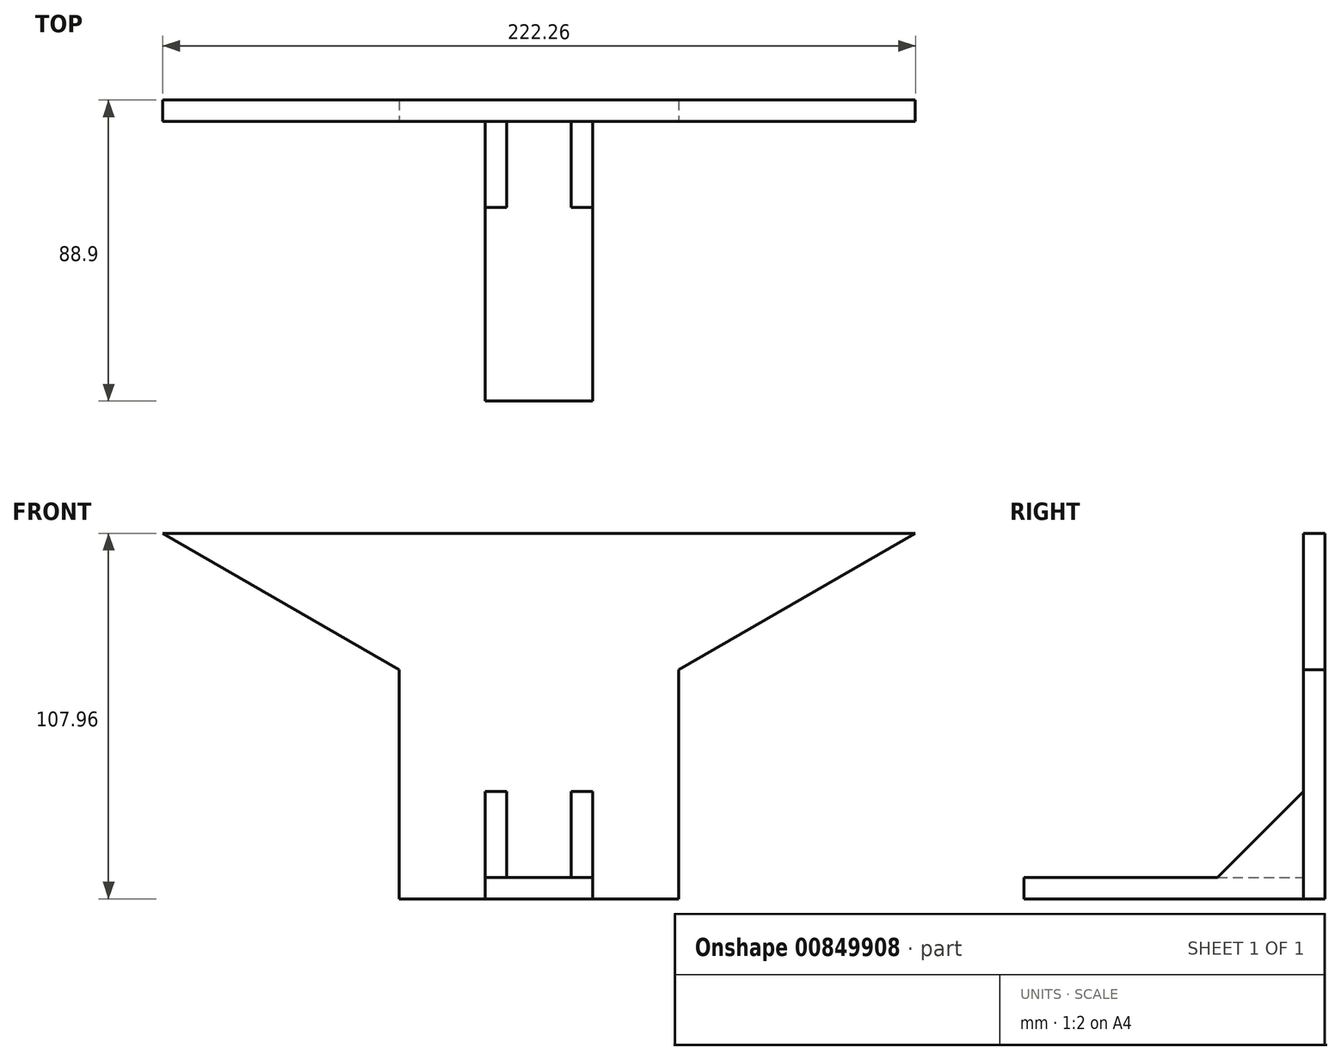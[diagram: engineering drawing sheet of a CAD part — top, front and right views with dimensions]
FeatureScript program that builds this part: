
annotation { "Feature Type Name" : "Feature", "Feature Type Description" : "" }
export const myFeature = defineFeature(function(context is Context, id is Id, definition is map)
    precondition{}
    {
        {
            var Q0;
            Q0=qCreatedBy(makeId("Front.planeOp"),FACE);
            var sketch = newSketch(context, id + "F0", { "sketchPlane" : qUnion([Q0])});
            skLineSegment(sketch, "E0.bottom", {"start": v(-41.28, 53.98) * mm, "end": v(0, 53.98) * mm});
            skLineSegment(sketch, "E0.top", {"start": v(-41.28, -53.98) * mm, "end": v(0, -53.98) * mm});
            skLineSegment(sketch, "E0.left", {"start": v(-41.28, 53.97) * mm, "end": v(-41.28, -53.98) * mm});
            skLineSegment(sketch, "E0.right", {"start": v(0, 53.98) * mm, "end": v(0, -53.98) * mm});
            skLineSegment(sketch, "E1", {"start": v(-41.28, 53.97) * mm, "end": v(-111.13, 53.97) * mm});
            skLineSegment(sketch, "E2", {"start": v(-111.12, 53.97) * mm, "end": v(-41.28, 13.65) * mm});
            skSolve(sketch);
        }
        {
            var Q0;
            {var subQ0=sQuery(id+"F0.wireOp",EDGE,"E1");Q0=makeQuery(id+"F0.imprint","IMPRINT",FACE,{"disambiguationData":[TD([[makeQuery(id+"F0.imprint","IMPRINT",EDGE,{"derivedFrom":subQ0}),1.0]])]});}
            var Q1;
            {var subQ3=sQuery(id+"F0.wireOp",EDGE,"E0.bottom");Q1=makeQuery(id+"F0.imprint","IMPRINT",FACE,{"disambiguationData":[TD([[makeQuery(id+"F0.imprint","IMPRINT",EDGE,{"derivedFrom":subQ3}),-1.0]])]});}
            extrude(context, id + "F1", {"entities" : qUnion([Q0, Q1]), "oppositeDirection" : true, "depth" : 6.35 * mm, "offsetDistance" : 25.4 * mm});
        }
        {
            var Q0;
            Q0=makeQuery(id+"F1.opExtrude","SWEPT_BODY",BODY,{"disambiguationData":[OSD([sQuery(id+"F0.wireOp",EDGE,"E0.bottom"),sQuery(id+"F0.wireOp",EDGE,"E0.top"),sQuery(id+"F0.wireOp",EDGE,"E0.left"),sQuery(id+"F0.wireOp",EDGE,"E0.right"),sQuery(id+"F0.wireOp",EDGE,"E1"),sQuery(id+"F0.wireOp",EDGE,"E2")])]});
            var Q1;
            Q1=qCreatedBy(makeId("Right.planeOp"),FACE);
            mirror(context, id + "F2", {"operationType" : NewBodyOperationType.ADD, "entities" : qUnion([Q0]), "mirrorPlane" : qUnion([Q1])});
        }
        {
            var Q0;
            Q0=qCreatedBy(makeId("Front.planeOp"),FACE);
            var sketch = newSketch(context, id + "F3", { "sketchPlane" : qUnion([Q0])});
            skLineSegment(sketch, "E3.bottom", {"start": v(-15.88, -47.62) * mm, "end": v(15.88, -47.62) * mm});
            skLineSegment(sketch, "E3.top", {"start": v(-15.88, -53.98) * mm, "end": v(15.88, -53.98) * mm});
            skLineSegment(sketch, "E3.left", {"start": v(-15.88, -47.62) * mm, "end": v(-15.88, -53.98) * mm});
            skLineSegment(sketch, "E3.right", {"start": v(15.88, -47.62) * mm, "end": v(15.88, -53.98) * mm});
            skSolve(sketch);
        }
        {
            var Q0;
            Q0 = qSketchRegion(id + "F3", true);
            extrude(context, id + "F4", {"entities" : qUnion([Q0]), "operationType" : NewBodyOperationType.ADD, "depth" : 82.55 * mm, "offsetDistance" : 25.4 * mm});
        }
        {
            var Q0;
            Q0=makeQuery(id+"F4.opExtrude","SWEPT_FACE",FACE,{"disambiguationData":[OSD([sQuery(id+"F3.wireOp",EDGE,"E3.right")])]});
            var sketch = newSketch(context, id + "F5", { "sketchPlane" : qUnion([Q0])});
            skLineSegment(sketch, "E4", {"start": v(-25.4, -47.62) * mm, "end": v(0, -22.22) * mm});
            skLineSegment(sketch, "E5", {"start": v(0, -22.22) * mm, "end": v(0, -47.62) * mm});
            skLineSegment(sketch, "E6", {"start": v(0, -47.62) * mm, "end": v(-25.4, -47.62) * mm});
            skSolve(sketch);
        }
        {
            var Q0;
            Q0 = qSketchRegion(id + "F5", true);
            extrude(context, id + "F6", {"entities" : qUnion([Q0]), "operationType" : NewBodyOperationType.ADD, "oppositeDirection" : true, "depth" : 6.35 * mm, "offsetDistance" : 25.4 * mm});
        }
        {
            var Q0;
            Q0=makeQuery(id+"F1.opExtrude","SWEPT_BODY",BODY,{"disambiguationData":[OSD([sQuery(id+"F0.wireOp",EDGE,"E0.bottom"),sQuery(id+"F0.wireOp",EDGE,"E0.top"),sQuery(id+"F0.wireOp",EDGE,"E0.left"),sQuery(id+"F0.wireOp",EDGE,"E0.right"),sQuery(id+"F0.wireOp",EDGE,"E1"),sQuery(id+"F0.wireOp",EDGE,"E2")])]});
            var Q1;
            Q1=qCreatedBy(makeId("Right.planeOp"),FACE);
            mirror(context, id + "F7", {"operationType" : NewBodyOperationType.ADD, "entities" : qUnion([Q0]), "mirrorPlane" : qUnion([Q1])});
        }
    });
